# Revit family: Gira_2003600
name_source: partatom
category: Elektroinstallationen
revit_build: Autodesk Revit 2017 (Build: 20160225_1515(x64)
units: mm (PartAtom-declared; Revit-internal decimal feet)

## family parameters
Basisbauteil = Fläche
Beim Laden mit Abzugskörper schneiden = Nein
Bemaßung runder Anschluss = Durchmesser verwenden
Beschriftungsausrichtung beibehalten = Ja
Gemeinsam genutzt = Nein
Raumberechnungspunkt = Nein
Teiletyp = Normal

## types (1)
- Tastsens.2 3f 24 V pot.frei BSF System 55 Edelstahl
    Andere Bussysteme = ohne
    Anzahl der Betätigungspunkte = 6
    Anzahl der Tasten = 3
    Ausführung der Oberfläche = nicht zutreffend
    BIM = https://media.stage.bim.site und Tasten.rfa
    BIMSITE_PRODUCT_ID = c37665e588a4d1d6b732b5195e1232502ac65da8
    Beschreibung = Tastsensor 2 3fach 24 V potenzialfrei mit Beschriftungsfeld  Edelstahl Merkmale: Tastsensor 2 zum Anschluss an 24 V Steuersysteme:  Drei Wippen mit je zwei roten LEDs zur Statusanzeige.  Demontageschutz durch Verschraubung.  Hintergrundbeleuchtung.  Anschluss von sechs Tastern, sechs LEDs und Hintergrundbeleuchtung über Klemmblock auf der Rückseite.  Hinweise :  Nur für SELV-Stromkreise geeignet.  Auch beleuchtet anschließbar.  Professionelle Beschriftung über den Gira Beschriftungsservice www.beschriftung.gira.de.
    Bussystem Funkbus = Ja
    Bussystem KNX = Ja
    Bussystem KNX-Funk = Nein
    Bussystem LON = Nein
    Bussystem Powernet = Nein
    Datenblatt = https://media.stage.bim.site
    Datenblatt 1 = https://media.stage.bim.site
    Farbe = Edelstahl
    GTIN = 4010337020363
    HAN = 2003600
    HeinzeBIM = https://www.heinze.de
    Hersteller = Gira
    Kosten = 0 $
    Mit Beschriftungsfeld = Ja
    Mit Busankopplung = Nein
    Mit Diebstahl-/Demontageschutz = Nein
    Mit Display = Nein
    Mit Infrarotsensor = Nein
    Mit LED-Anzeige = Ja
    Mit Raumthermostat = Nein
    Montageart = Unterputz
    Oberfläche Text = lackiert
    Produktseite = https://media.stage.bim.site
    Schutzart (IP) = IP20
    Transparent = Nein
    Typname = Tastsens.2 3f 24 V pot.frei BSF System 55 Edelstahl
    URL = https://www.gira.de
    Vorgabe-Ansicht = 1219 mm
    Werkstoff Text = sonstige
    Werkstoffgüte = sonstige

## geometry (parser evidence)
native form markers: Sweep x11
no freeform markers — native parametric forms only
